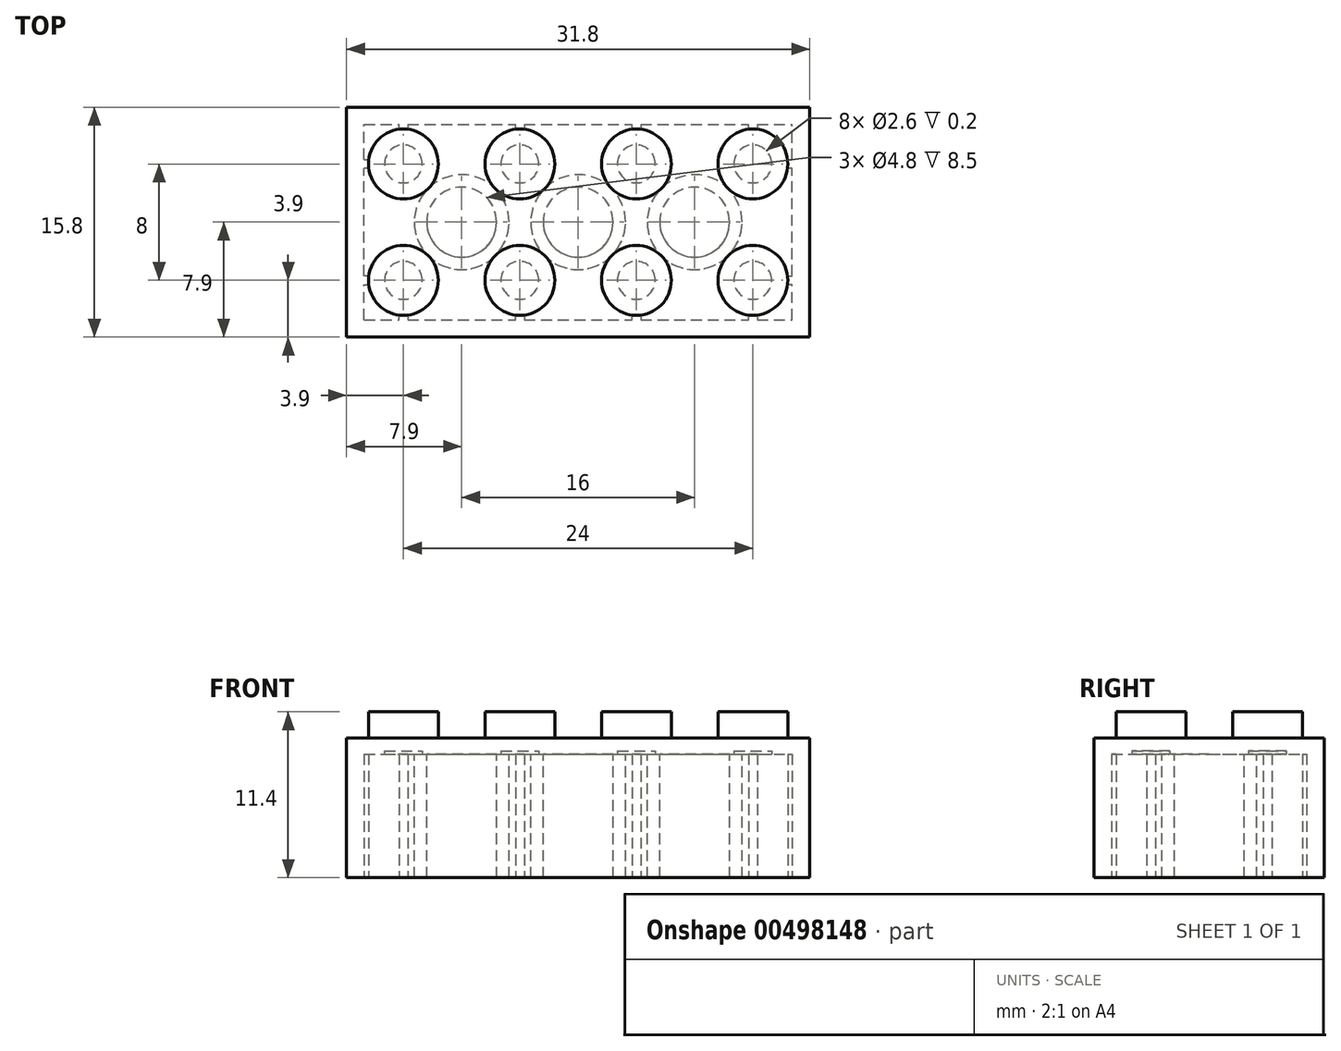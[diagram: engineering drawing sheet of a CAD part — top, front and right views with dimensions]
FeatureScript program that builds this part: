
annotation { "Feature Type Name" : "Feature", "Feature Type Description" : "" }
export const myFeature = defineFeature(function(context is Context, id is Id, definition is map)
    precondition{}
    {
        {
            var Q0;
            Q0=qCreatedBy(makeId("Top.planeOp"),FACE);
            var sketch = newSketch(context, id + "F0", { "sketchPlane" : qUnion([Q0])});
            skLineSegment(sketch, "E0.bottom", {"start": v(-15.9, 7.9) * mm, "end": v(15.9, 7.9) * mm});
            skLineSegment(sketch, "E0.top", {"start": v(-15.9, -7.9) * mm, "end": v(15.9, -7.9) * mm});
            skLineSegment(sketch, "E0.left", {"start": v(-15.9, 7.9) * mm, "end": v(-15.9, -7.9) * mm});
            skLineSegment(sketch, "E0.right", {"start": v(15.9, 7.9) * mm, "end": v(15.9, -7.9) * mm});
            skSolve(sketch);
        }
        {
            var Q0;
            Q0 = qSketchRegion(id + "F0", true);
            extrude(context, id + "F1", {"entities" : qUnion([Q0]), "depth" : 9.6 * mm});
        }
        {
            var Q0;
            Q0=makeQuery(id+"F1.opExtrude","CAP_FACE",FACE,{"disambiguationData":[OSD([sQuery(id+"F0.wireOp",EDGE,"E0.bottom"),sQuery(id+"F0.wireOp",EDGE,"E0.top"),sQuery(id+"F0.wireOp",EDGE,"E0.left"),sQuery(id+"F0.wireOp",EDGE,"E0.right")])],"isStart":false});
            var sketch = newSketch(context, id + "F2", { "sketchPlane" : qUnion([Q0])});
            skCircle(sketch, "E1", {"center": v(-12, 4) * mm, "radius": 2.4 * mm});
            skCircle(sketch, "E2", {"center": v(-12, -4) * mm, "radius": 2.4 * mm});
            skCircle(sketch, "E3.1.0.0", {"center": v(-4, 4) * mm, "radius": 2.4 * mm});
            skCircle(sketch, "E3.2.0.0", {"center": v(4, 4) * mm, "radius": 2.4 * mm});
            skCircle(sketch, "E3.3.0.0", {"center": v(12, 4) * mm, "radius": 2.4 * mm});
            skLineSegment(sketch, "E3.direction1", {"start": v(-12, 4) * mm, "end": v(-4, 4) * mm, "construction": true});
            skCircle(sketch, "E4.1.0.0", {"center": v(-4, -4) * mm, "radius": 2.4 * mm});
            skCircle(sketch, "E4.2.0.0", {"center": v(4, -4) * mm, "radius": 2.4 * mm});
            skCircle(sketch, "E4.3.0.0", {"center": v(12, -4) * mm, "radius": 2.4 * mm});
            skLineSegment(sketch, "E4.direction1", {"start": v(-12, -4) * mm, "end": v(-4, -4) * mm, "construction": true});
            skSolve(sketch);
        }
        {
            var Q0;
            Q0=makeQuery(id+"F2.imprint","IMPRINT",FACE,{"disambiguationData":[TD([[makeQuery(id+"F2.imprint","IMPRINT",EDGE,{"derivedFrom":sQuery(id+"F2.wireOp",EDGE,"E1")}),1.0]])]});
            var Q1;
            Q1=makeQuery(id+"F2.imprint","IMPRINT",FACE,{"disambiguationData":[TD([[makeQuery(id+"F2.imprint","IMPRINT",EDGE,{"derivedFrom":sQuery(id+"F2.wireOp",EDGE,"E3.1.0.0")}),1.0]])]});
            var Q2;
            Q2=makeQuery(id+"F2.imprint","IMPRINT",FACE,{"disambiguationData":[TD([[makeQuery(id+"F2.imprint","IMPRINT",EDGE,{"derivedFrom":sQuery(id+"F2.wireOp",EDGE,"E3.2.0.0")}),1.0]])]});
            var Q3;
            Q3=makeQuery(id+"F2.imprint","IMPRINT",FACE,{"disambiguationData":[TD([[makeQuery(id+"F2.imprint","IMPRINT",EDGE,{"derivedFrom":sQuery(id+"F2.wireOp",EDGE,"E3.3.0.0")}),1.0]])]});
            var Q4;
            Q4=makeQuery(id+"F2.imprint","IMPRINT",FACE,{"disambiguationData":[TD([[makeQuery(id+"F2.imprint","IMPRINT",EDGE,{"derivedFrom":sQuery(id+"F2.wireOp",EDGE,"E4.3.0.0")}),1.0]])]});
            var Q5;
            Q5=makeQuery(id+"F2.imprint","IMPRINT",FACE,{"disambiguationData":[TD([[makeQuery(id+"F2.imprint","IMPRINT",EDGE,{"derivedFrom":sQuery(id+"F2.wireOp",EDGE,"E4.2.0.0")}),1.0]])]});
            var Q6;
            Q6=makeQuery(id+"F2.imprint","IMPRINT",FACE,{"disambiguationData":[TD([[makeQuery(id+"F2.imprint","IMPRINT",EDGE,{"derivedFrom":sQuery(id+"F2.wireOp",EDGE,"E4.1.0.0")}),1.0]])]});
            var Q7;
            Q7=makeQuery(id+"F2.imprint","IMPRINT",FACE,{"disambiguationData":[TD([[makeQuery(id+"F2.imprint","IMPRINT",EDGE,{"derivedFrom":sQuery(id+"F2.wireOp",EDGE,"E2")}),1.0]])]});
            extrude(context, id + "F3", {"entities" : qUnion([Q0, Q1, Q2, Q3, Q4, Q5, Q6, Q7]), "operationType" : NewBodyOperationType.ADD, "depth" : 1.8 * mm});
        }
        {
            var Q0;
            Q0=makeQuery(id+"F1.opExtrude","CAP_FACE",FACE,{"disambiguationData":[OSD([sQuery(id+"F0.wireOp",EDGE,"E0.bottom"),sQuery(id+"F0.wireOp",EDGE,"E0.top"),sQuery(id+"F0.wireOp",EDGE,"E0.left"),sQuery(id+"F0.wireOp",EDGE,"E0.right")])],"isStart":true});
            var sketch = newSketch(context, id + "F4", { "sketchPlane" : qUnion([Q0])});
            skLineSegment(sketch, "E5.bottom", {"start": v(-14.7, 6.7) * mm, "end": v(-12.3, 6.7) * mm});
            skLineSegment(sketch, "E5.top", {"start": v(-14.7, -6.7) * mm, "end": v(-12.3, -6.7) * mm});
            skLineSegment(sketch, "E5.left", {"start": v(-14.7, 6.7) * mm, "end": v(-14.7, 4.3) * mm});
            skLineSegment(sketch, "E5.right", {"start": v(14.7, 6.7) * mm, "end": v(14.7, 4.3) * mm});
            skCircle(sketch, "E6", {"center": v(-12, 4) * mm, "radius": 1.3 * mm});
            skCircle(sketch, "E7.1.0.0", {"center": v(-4, 4) * mm, "radius": 1.3 * mm});
            skCircle(sketch, "E7.2.0.0", {"center": v(4, 4) * mm, "radius": 1.3 * mm});
            skCircle(sketch, "E7.3.0.0", {"center": v(12, 4) * mm, "radius": 1.3 * mm});
            skLineSegment(sketch, "E7.direction1", {"start": v(-12, 4) * mm, "end": v(-4, 4) * mm, "construction": true});
            skCircle(sketch, "E8", {"center": v(-12, -4) * mm, "radius": 1.3 * mm});
            skCircle(sketch, "E9.1.0.0", {"center": v(-4, -4) * mm, "radius": 1.3 * mm});
            skCircle(sketch, "E9.2.0.0", {"center": v(4, -4) * mm, "radius": 1.3 * mm});
            skCircle(sketch, "E9.3.0.0", {"center": v(12, -4) * mm, "radius": 1.3 * mm});
            skLineSegment(sketch, "E9.direction1", {"start": v(-12, -4) * mm, "end": v(-4, -4) * mm, "construction": true});
            skLineSegment(sketch, "E10", {"start": v(14.7, 4.3) * mm, "end": v(14.4, 4.3) * mm});
            skLineSegment(sketch, "E11", {"start": v(14.4, 4.3) * mm, "end": v(14.4, 3.7) * mm});
            skLineSegment(sketch, "E12", {"start": v(14.4, 3.7) * mm, "end": v(14.7, 3.7) * mm});
            skLineSegment(sketch, "E13.trimOffspring", {"start": v(14.7, 3.7) * mm, "end": v(14.7, -3.7) * mm});
            skLineSegment(sketch, "E14", {"start": v(11.7, 6.7) * mm, "end": v(11.7, 6.4) * mm});
            skLineSegment(sketch, "E15", {"start": v(11.7, 6.4) * mm, "end": v(12.3, 6.4) * mm});
            skLineSegment(sketch, "E16", {"start": v(12.3, 6.4) * mm, "end": v(12.3, 6.7) * mm});
            skLineSegment(sketch, "E17.trimOffspring", {"start": v(12.3, 6.7) * mm, "end": v(14.7, 6.7) * mm});
            skLineSegment(sketch, "E18.1.0.0", {"start": v(3.7, 6.7) * mm, "end": v(3.7, 6.4) * mm});
            skLineSegment(sketch, "E18.1.0.1", {"start": v(3.7, 6.4) * mm, "end": v(4.3, 6.4) * mm});
            skLineSegment(sketch, "E18.1.0.2", {"start": v(4.3, 6.4) * mm, "end": v(4.3, 6.7) * mm});
            skLineSegment(sketch, "E18.2.0.0", {"start": v(-4.3, 6.7) * mm, "end": v(-4.3, 6.4) * mm});
            skLineSegment(sketch, "E18.2.0.1", {"start": v(-4.3, 6.4) * mm, "end": v(-3.7, 6.4) * mm});
            skLineSegment(sketch, "E18.2.0.2", {"start": v(-3.7, 6.4) * mm, "end": v(-3.7, 6.7) * mm});
            skLineSegment(sketch, "E18.3.0.0", {"start": v(-12.3, 6.7) * mm, "end": v(-12.3, 6.4) * mm});
            skLineSegment(sketch, "E18.3.0.1", {"start": v(-12.3, 6.4) * mm, "end": v(-11.7, 6.4) * mm});
            skLineSegment(sketch, "E18.3.0.2", {"start": v(-11.7, 6.4) * mm, "end": v(-11.7, 6.7) * mm});
            skLineSegment(sketch, "E18.direction1", {"start": v(11.7, 6.4) * mm, "end": v(3.7, 6.4) * mm, "construction": true});
            skLineSegment(sketch, "E19.trimOffspring", {"start": v(4.3, 6.7) * mm, "end": v(11.7, 6.7) * mm});
            skLineSegment(sketch, "E20.trimOffspring", {"start": v(-3.7, 6.7) * mm, "end": v(3.7, 6.7) * mm});
            skLineSegment(sketch, "E21.trimOffspring", {"start": v(-11.7, 6.7) * mm, "end": v(-4.3, 6.7) * mm});
            skLineSegment(sketch, "E22", {"start": v(14.7, -3.7) * mm, "end": v(14.4, -3.7) * mm});
            skLineSegment(sketch, "E23", {"start": v(14.4, -3.7) * mm, "end": v(14.4, -4.3) * mm});
            skLineSegment(sketch, "E24", {"start": v(14.4, -4.3) * mm, "end": v(14.7, -4.3) * mm});
            skLineSegment(sketch, "E25.trimOffspring", {"start": v(14.7, -4.3) * mm, "end": v(14.7, -6.7) * mm});
            skLineSegment(sketch, "E26", {"start": v(12.3, -6.7) * mm, "end": v(12.3, -6.4) * mm});
            skLineSegment(sketch, "E27", {"start": v(12.3, -6.4) * mm, "end": v(11.7, -6.4) * mm});
            skLineSegment(sketch, "E28", {"start": v(11.7, -6.4) * mm, "end": v(11.7, -6.7) * mm});
            skLineSegment(sketch, "E29.trimOffspring", {"start": v(12.3, -6.7) * mm, "end": v(14.7, -6.7) * mm});
            skLineSegment(sketch, "E30.1.0.0", {"start": v(3.7, -6.4) * mm, "end": v(3.7, -6.7) * mm});
            skLineSegment(sketch, "E30.1.0.1", {"start": v(4.3, -6.4) * mm, "end": v(3.7, -6.4) * mm});
            skLineSegment(sketch, "E30.1.0.2", {"start": v(4.3, -6.7) * mm, "end": v(4.3, -6.4) * mm});
            skLineSegment(sketch, "E30.2.0.0", {"start": v(-4.3, -6.4) * mm, "end": v(-4.3, -6.7) * mm});
            skLineSegment(sketch, "E30.2.0.1", {"start": v(-3.7, -6.4) * mm, "end": v(-4.3, -6.4) * mm});
            skLineSegment(sketch, "E30.2.0.2", {"start": v(-3.7, -6.7) * mm, "end": v(-3.7, -6.4) * mm});
            skLineSegment(sketch, "E30.3.0.0", {"start": v(-12.3, -6.4) * mm, "end": v(-12.3, -6.7) * mm});
            skLineSegment(sketch, "E30.3.0.1", {"start": v(-11.7, -6.4) * mm, "end": v(-12.3, -6.4) * mm});
            skLineSegment(sketch, "E30.3.0.2", {"start": v(-11.7, -6.7) * mm, "end": v(-11.7, -6.4) * mm});
            skLineSegment(sketch, "E30.direction1", {"start": v(11.7, -6.7) * mm, "end": v(4.3, -6.7) * mm, "construction": true});
            skLineSegment(sketch, "E31.trimOffspring", {"start": v(-3.7, -6.7) * mm, "end": v(3.7, -6.7) * mm});
            skLineSegment(sketch, "E32.trimOffspring", {"start": v(-11.7, -6.7) * mm, "end": v(-4.3, -6.7) * mm});
            skLineSegment(sketch, "E33", {"start": v(-14.7, -4.3) * mm, "end": v(-14.4, -4.3) * mm});
            skLineSegment(sketch, "E34", {"start": v(-14.4, -4.3) * mm, "end": v(-14.4, -3.7) * mm});
            skLineSegment(sketch, "E35", {"start": v(-14.4, -3.7) * mm, "end": v(-14.7, -3.7) * mm});
            skLineSegment(sketch, "E36", {"start": v(-14.7, 4.3) * mm, "end": v(-14.4, 4.3) * mm});
            skLineSegment(sketch, "E37", {"start": v(-14.4, 4.3) * mm, "end": v(-14.4, 3.7) * mm});
            skLineSegment(sketch, "E38", {"start": v(-14.4, 3.7) * mm, "end": v(-14.7, 3.7) * mm});
            skLineSegment(sketch, "E39.trimOffspring", {"start": v(-14.7, 3.7) * mm, "end": v(-14.7, -3.7) * mm});
            skLineSegment(sketch, "E40.trimOffspring", {"start": v(-14.7, -4.3) * mm, "end": v(-14.7, -6.7) * mm});
            skLineSegment(sketch, "E41.trimOffspring", {"start": v(4.3, -6.7) * mm, "end": v(11.7, -6.7) * mm});
            skSolve(sketch);
        }
        {
            var Q0;
            Q0=makeQuery(id+"F4.imprint","IMPRINT",FACE,{"disambiguationData":[TD([[makeQuery(id+"F4.imprint","IMPRINT",EDGE,{"derivedFrom":sQuery(id+"F4.wireOp",EDGE,"E6")}),1.0]])]});
            var Q1;
            Q1=makeQuery(id+"F4.imprint","IMPRINT",FACE,{"disambiguationData":[TD([[makeQuery(id+"F4.imprint","IMPRINT",EDGE,{"derivedFrom":sQuery(id+"F4.wireOp",EDGE,"E7.1.0.0")}),1.0]])]});
            var Q2;
            Q2=makeQuery(id+"F4.imprint","IMPRINT",FACE,{"disambiguationData":[TD([[makeQuery(id+"F4.imprint","IMPRINT",EDGE,{"derivedFrom":sQuery(id+"F4.wireOp",EDGE,"E7.2.0.0")}),1.0]])]});
            var Q3;
            Q3=makeQuery(id+"F4.imprint","IMPRINT",FACE,{"disambiguationData":[TD([[makeQuery(id+"F4.imprint","IMPRINT",EDGE,{"derivedFrom":sQuery(id+"F4.wireOp",EDGE,"E7.3.0.0")}),1.0]])]});
            var Q4;
            Q4=makeQuery(id+"F4.imprint","IMPRINT",FACE,{"disambiguationData":[TD([[makeQuery(id+"F4.imprint","IMPRINT",EDGE,{"derivedFrom":sQuery(id+"F4.wireOp",EDGE,"E9.3.0.0")}),1.0]])]});
            var Q5;
            Q5=makeQuery(id+"F4.imprint","IMPRINT",FACE,{"disambiguationData":[TD([[makeQuery(id+"F4.imprint","IMPRINT",EDGE,{"derivedFrom":sQuery(id+"F4.wireOp",EDGE,"E9.2.0.0")}),1.0]])]});
            var Q6;
            Q6=makeQuery(id+"F4.imprint","IMPRINT",FACE,{"disambiguationData":[TD([[makeQuery(id+"F4.imprint","IMPRINT",EDGE,{"derivedFrom":sQuery(id+"F4.wireOp",EDGE,"E9.1.0.0")}),1.0]])]});
            var Q7;
            Q7=makeQuery(id+"F4.imprint","IMPRINT",FACE,{"disambiguationData":[TD([[makeQuery(id+"F4.imprint","IMPRINT",EDGE,{"derivedFrom":sQuery(id+"F4.wireOp",EDGE,"E8")}),1.0]])]});
            extrude(context, id + "F5", {"entities" : qUnion([Q0, Q1, Q2, Q3, Q4, Q5, Q6, Q7]), "operationType" : NewBodyOperationType.REMOVE, "oppositeDirection" : true, "depth" : 8.7 * mm});
        }
        {
            var Q0;
            Q0 = qSketchRegion(id + "F4", true);
            extrude(context, id + "F6", {"entities" : qUnion([Q0]), "operationType" : NewBodyOperationType.REMOVE, "oppositeDirection" : true, "depth" : 8.5 * mm});
        }
        {
            var Q0;
            Q0=makeQuery(id+"F6.boolean.opBoolean","COPY",FACE,{"derivedFrom":makeQuery(id+"F6.opExtrude","CAP_FACE",FACE,{"disambiguationData":[OSD([sQuery(id+"F4.wireOp",EDGE,"E5.bottom"),sQuery(id+"F4.wireOp",EDGE,"E5.top"),sQuery(id+"F4.wireOp",EDGE,"E5.left"),sQuery(id+"F4.wireOp",EDGE,"E5.right"),sQuery(id+"F4.wireOp",EDGE,"E7.2.0.0"),sQuery(id+"F4.wireOp",EDGE,"E7.3.0.0"),sQuery(id+"F4.wireOp",EDGE,"E8"),sQuery(id+"F4.wireOp",EDGE,"E9.1.0.0"),sQuery(id+"F4.wireOp",EDGE,"E9.2.0.0"),sQuery(id+"F4.wireOp",EDGE,"E9.3.0.0"),sQuery(id+"F4.wireOp",EDGE,"E10"),sQuery(id+"F4.wireOp",EDGE,"E11"),sQuery(id+"F4.wireOp",EDGE,"E12"),sQuery(id+"F4.wireOp",EDGE,"E13.trimOffspring"),sQuery(id+"F4.wireOp",EDGE,"E14"),sQuery(id+"F4.wireOp",EDGE,"E15"),sQuery(id+"F4.wireOp",EDGE,"E16"),sQuery(id+"F4.wireOp",EDGE,"E17.trimOffspring"),sQuery(id+"F4.wireOp",EDGE,"E18.1.0.0"),sQuery(id+"F4.wireOp",EDGE,"E18.1.0.1"),sQuery(id+"F4.wireOp",EDGE,"E18.1.0.2"),sQuery(id+"F4.wireOp",EDGE,"E7.1.0.0"),sQuery(id+"F4.wireOp",EDGE,"E18.2.0.0"),sQuery(id+"F4.wireOp",EDGE,"E18.2.0.1"),sQuery(id+"F4.wireOp",EDGE,"E18.2.0.2"),sQuery(id+"F4.wireOp",EDGE,"E6"),sQuery(id+"F4.wireOp",EDGE,"E18.3.0.0"),sQuery(id+"F4.wireOp",EDGE,"E18.3.0.1"),sQuery(id+"F4.wireOp",EDGE,"E18.3.0.2"),sQuery(id+"F4.wireOp",EDGE,"E19.trimOffspring"),sQuery(id+"F4.wireOp",EDGE,"E20.trimOffspring"),sQuery(id+"F4.wireOp",EDGE,"E21.trimOffspring"),sQuery(id+"F4.wireOp",EDGE,"E22"),sQuery(id+"F4.wireOp",EDGE,"E23"),sQuery(id+"F4.wireOp",EDGE,"E24"),sQuery(id+"F4.wireOp",EDGE,"E25.trimOffspring"),sQuery(id+"F4.wireOp",EDGE,"E26"),sQuery(id+"F4.wireOp",EDGE,"E27"),sQuery(id+"F4.wireOp",EDGE,"E28"),sQuery(id+"F4.wireOp",EDGE,"E29.trimOffspring"),sQuery(id+"F4.wireOp",EDGE,"E30.1.0.0"),sQuery(id+"F4.wireOp",EDGE,"E30.1.0.1"),sQuery(id+"F4.wireOp",EDGE,"E30.1.0.2"),sQuery(id+"F4.wireOp",EDGE,"E30.2.0.0"),sQuery(id+"F4.wireOp",EDGE,"E30.2.0.1"),sQuery(id+"F4.wireOp",EDGE,"E30.2.0.2"),sQuery(id+"F4.wireOp",EDGE,"E30.3.0.0"),sQuery(id+"F4.wireOp",EDGE,"E30.3.0.1"),sQuery(id+"F4.wireOp",EDGE,"E30.3.0.2"),sQuery(id+"F4.wireOp",EDGE,"E31.trimOffspring"),sQuery(id+"F4.wireOp",EDGE,"E32.trimOffspring"),sQuery(id+"F4.wireOp",EDGE,"E33"),sQuery(id+"F4.wireOp",EDGE,"E34"),sQuery(id+"F4.wireOp",EDGE,"E35"),sQuery(id+"F4.wireOp",EDGE,"E36"),sQuery(id+"F4.wireOp",EDGE,"E37"),sQuery(id+"F4.wireOp",EDGE,"E38"),sQuery(id+"F4.wireOp",EDGE,"E39.trimOffspring"),sQuery(id+"F4.wireOp",EDGE,"E40.trimOffspring"),sQuery(id+"F4.wireOp",EDGE,"E41.trimOffspring")])],"isStart":false})});
            var sketch = newSketch(context, id + "F7", { "sketchPlane" : qUnion([Q0])});
            skLineSegment(sketch, "E42", {"start": v(-12, 4) * mm, "end": v(-12, -4) * mm, "construction": true});
            skLineSegment(sketch, "E43", {"start": v(-4, 4) * mm, "end": v(-4, -4) * mm, "construction": true});
            skLineSegment(sketch, "E44", {"start": v(4, 4) * mm, "end": v(4, -4) * mm, "construction": true});
            skLineSegment(sketch, "E45", {"start": v(12, 4) * mm, "end": v(12, -4) * mm, "construction": true});
            skLineSegment(sketch, "E46", {"start": v(-12, 0) * mm, "end": v(12, 0) * mm, "construction": true});
            skCircle(sketch, "E47", {"center": v(-8, 0) * mm, "radius": 2.4 * mm});
            skCircle(sketch, "E48", {"center": v(-8, 0) * mm, "radius": 3.26 * mm});
            skCircle(sketch, "E49.1.0.0", {"center": v(0, 0) * mm, "radius": 3.26 * mm});
            skCircle(sketch, "E49.1.0.1", {"center": v(0, 0) * mm, "radius": 2.4 * mm});
            skCircle(sketch, "E49.2.0.0", {"center": v(8, 0) * mm, "radius": 3.26 * mm});
            skCircle(sketch, "E49.2.0.1", {"center": v(8, 0) * mm, "radius": 2.4 * mm});
            skLineSegment(sketch, "E49.direction1", {"start": v(-8, 0) * mm, "end": v(0, 0) * mm, "construction": true});
            skSolve(sketch);
        }
        {
            var Q0;
            Q0=makeQuery(id+"F7.imprint","IMPRINT",FACE,{"disambiguationData":[TD([[makeQuery(id+"F7.imprint","IMPRINT",EDGE,{"derivedFrom":sQuery(id+"F7.wireOp",EDGE,"E49.1.0.0")}),1.0]])]});
            var Q1;
            Q1=makeQuery(id+"F7.imprint","IMPRINT",FACE,{"disambiguationData":[TD([[makeQuery(id+"F7.imprint","IMPRINT",EDGE,{"derivedFrom":sQuery(id+"F7.wireOp",EDGE,"E49.2.0.0")}),1.0]])]});
            var Q2;
            Q2=makeQuery(id+"F7.imprint","IMPRINT",FACE,{"disambiguationData":[TD([[makeQuery(id+"F7.imprint","IMPRINT",EDGE,{"derivedFrom":sQuery(id+"F7.wireOp",EDGE,"E47")}),-1.0]])]});
            var Q3;
            Q3=makeQuery(id+"F1.opExtrude","CAP_FACE",FACE,{"disambiguationData":[OSD([sQuery(id+"F0.wireOp",EDGE,"E0.bottom"),sQuery(id+"F0.wireOp",EDGE,"E0.top"),sQuery(id+"F0.wireOp",EDGE,"E0.left"),sQuery(id+"F0.wireOp",EDGE,"E0.right")])],"isStart":true});
            extrude(context, id + "F8", {"entities" : qUnion([Q0, Q1, Q2]), "operationType" : NewBodyOperationType.ADD, "endBound" : BoundingType.UP_TO_SURFACE, "endBoundEntityFace" : qUnion([Q3]), "depth" : 25 * mm});
        }
    });
